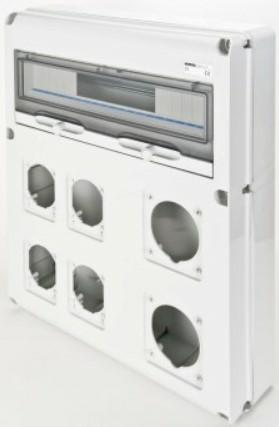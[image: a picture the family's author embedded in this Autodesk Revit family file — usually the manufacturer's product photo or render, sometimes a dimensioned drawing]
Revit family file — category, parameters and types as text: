
# Revit family: Building-IEC309Boards-GEWISS-68QDIN-DISTRIBUTION-BOARD-20MOD_6SOCKET-OUTLETS
name_source: partatom
category: Apparecchi elettrici
units: mm (PartAtom-declared; Revit-internal decimal feet)

## family parameters
Condiviso = No
Host = Superficie
Mantenere orientamento annotazione = Sì
Punto di calcolo locali = Sì
Quota connettore circolare = Usa diametro
Taglio con vuoti quando caricato = No
Tipo di parte = Normale

## types (1)
- GW68021N - Q-DIN 20M 2S.O.63A 4S.O.16/32A IP65
    Accordance with Standards = EN 60208 - EN 60670-1 - IEC 60670-24
    Catalogue = BUILDING
    Catalogue Range = 68 QDIN
    Colour = Grey RAL 7035
    Descrizione = Q-DIN 20M 2S.O.63A 4S.O.16/32A IP65
    Dispersible power A (W) = 30
    Dispersible power B (W) = 92
    EAN code = 8011564744882
    Electrocod = 2242
    Glow Wire Test = 650°C
    Houseable socket = 2 IEC 309 63A - 4 IEC 309 16/32A
    IDF = 7fc76941-0cea-4757-b7ec-a7896b62d45f
    IDT = c4e5c53f-a295-41ab-9992-af314b14205a
    IP degree = IP65
    Immagine tipo = GW68021N.jpg
    Installation type = Surface-mounting
    Insulation class = II
    L_Moduli = 380 mm  [stored 1.24672 ft]
    Modello = GW68021N
    N_Moduli = 20 mm  [stored 0.0656168 ft]
    No. of modules EN 50022 = 20
    No. of provided blank lids = 2 IEC 309 16/32A+1 63A
    Operating temperature: = -25 +40 °C
    POMELLO = bianco
    PRESA = rosso
    Produttore = GEWISS S.p.A.
    Prospetto di default = 1219 mm
    SEO = Board
    STRUTTURA = RAL - 7035
    STRUTTURA ALTA = Poche
    Shock resistance = IK08
    Spostamento_S = 1000 mm  [stored 3.28084 ft]
    Technical sheet = https://www.gewiss.com
    Thermo-pressure with ball = 70
    URL = https://www.gewiss.com
    VETRO = Vetro
    Version file RFA = 21.5
    Version type = Empty

note: source unit labels omitted for Thermo-pressure with ball — the stored unit's dimension contradicts the parameter name (converter mislabeling)

note: [stored X ft] marks values corroborated as IEEE doubles in the binary element streams (Revit-internal decimal feet)

## geometry (parser evidence)
native form markers: Sweep x5
no freeform markers — native parametric forms only
